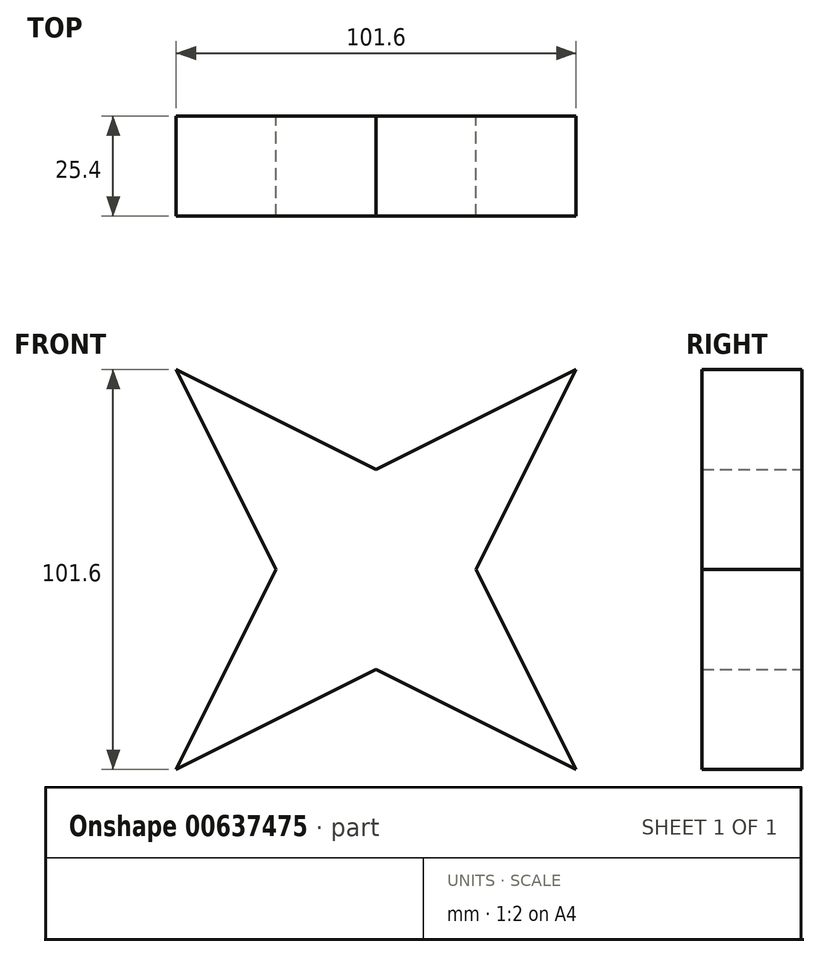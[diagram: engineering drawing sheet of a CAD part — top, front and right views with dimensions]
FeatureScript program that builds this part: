
annotation { "Feature Type Name" : "Feature", "Feature Type Description" : "" }
export const myFeature = defineFeature(function(context is Context, id is Id, definition is map)
    precondition{}
    {
        {
            var Q0;
            Q0=qCreatedBy(makeId("Front.planeOp"),FACE);
            var sketch = newSketch(context, id + "F0", { "sketchPlane" : qUnion([Q0])});
            skLineSegment(sketch, "E0", {"start": v(-50.8, 50.8) * mm, "end": v(-25.4, 0) * mm});
            skLineSegment(sketch, "E1", {"start": v(-25.4, 0) * mm, "end": v(-50.8, -50.8) * mm});
            skLineSegment(sketch, "E2", {"start": v(-50.8, -50.8) * mm, "end": v(0, -25.4) * mm});
            skLineSegment(sketch, "E3", {"start": v(0, -25.4) * mm, "end": v(50.8, -50.8) * mm});
            skLineSegment(sketch, "E4", {"start": v(25.4, 0) * mm, "end": v(50.8, 50.8) * mm});
            skLineSegment(sketch, "E5", {"start": v(50.8, 50.8) * mm, "end": v(0, 25.4) * mm});
            skLineSegment(sketch, "E6", {"start": v(0, 25.4) * mm, "end": v(-50.8, 50.8) * mm});
            skLineSegment(sketch, "E7", {"start": v(25.4, 0) * mm, "end": v(50.8, -50.8) * mm});
            skSolve(sketch);
        }
        {
            var Q0;
            Q0=makeQuery(id+"F0.imprint","IMPRINT",FACE,{"disambiguationData":[TD([[makeQuery(id+"F0.imprint","IMPRINT",EDGE,{"derivedFrom":sQuery(id+"F0.wireOp",EDGE,"E0")}),1.0]])]});
            extrude(context, id + "F1", {"entities" : qUnion([Q0]), "endBound" : BoundingType.SYMMETRIC, "depth" : 25.4 * mm, "offsetDistance" : 25.4 * mm});
        }
    });
